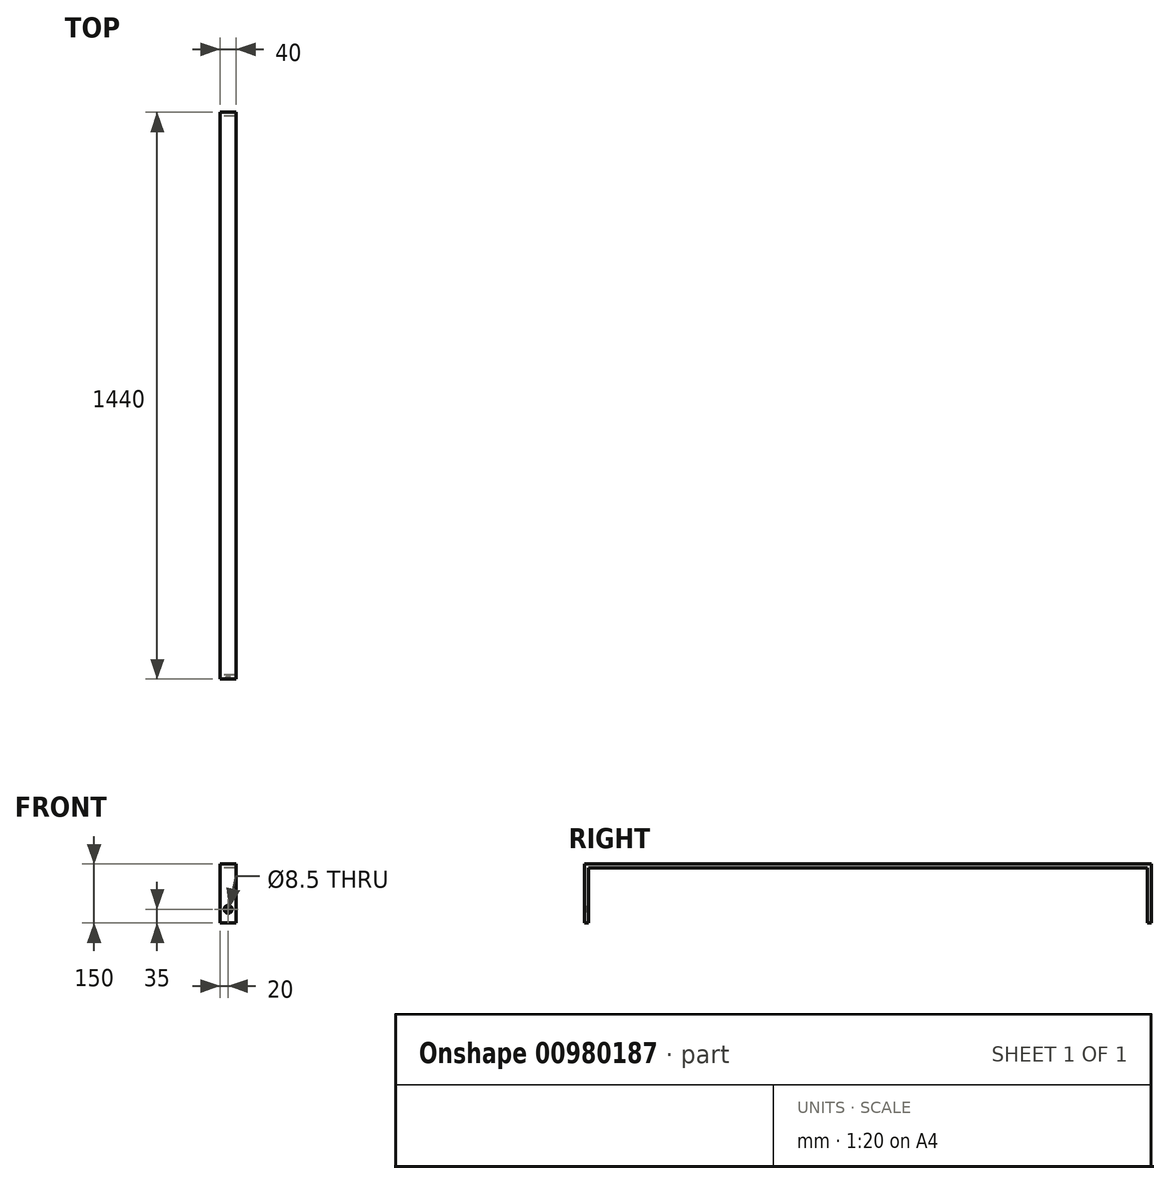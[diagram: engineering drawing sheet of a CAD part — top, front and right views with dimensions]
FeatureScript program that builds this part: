
annotation { "Feature Type Name" : "Feature", "Feature Type Description" : "" }
export const myFeature = defineFeature(function(context is Context, id is Id, definition is map)
    precondition{}
    {
        {
            var Q0;
            Q0=qCreatedBy(makeId("Right.planeOp"),FACE);
            var sketch = newSketch(context, id + "F0", { "sketchPlane" : qUnion([Q0])});
            skLineSegment(sketch, "E0", {"start": v(0, 0) * mm, "end": v(-720, 0) * mm});
            skLineSegment(sketch, "E1", {"start": v(-720, 0) * mm, "end": v(-720, -150) * mm});
            skLineSegment(sketch, "E2", {"start": v(-720, -150) * mm, "end": v(-710, -150) * mm});
            skLineSegment(sketch, "E3", {"start": v(-710, -150) * mm, "end": v(-710, -10) * mm});
            skLineSegment(sketch, "E4", {"start": v(-710, -10) * mm, "end": v(0, -10) * mm});
            skLineSegment(sketch, "E5.MirrorCS", {"start": v(720, -150) * mm, "end": v(710, -150) * mm});
            skLineSegment(sketch, "E6.MirrorCS", {"start": v(710, -150) * mm, "end": v(710, -10) * mm});
            skLineSegment(sketch, "E7.MirrorCS", {"start": v(710, -10) * mm, "end": v(0, -10) * mm});
            skLineSegment(sketch, "E8.MirrorCS", {"start": v(720, 0) * mm, "end": v(720, -150) * mm});
            skLineSegment(sketch, "E9.MirrorCS", {"start": v(0, 0) * mm, "end": v(720, 0) * mm});
            skSolve(sketch);
        }
        {
            var Q0;
            Q0=makeQuery(id+"F0.imprint","IMPRINT",FACE,{"disambiguationData":[TD([[makeQuery(id+"F0.imprint","IMPRINT",EDGE,{"derivedFrom":sQuery(id+"F0.wireOp",EDGE,"E0")}),1.0]])]});
            extrude(context, id + "F1", {"entities" : qUnion([Q0]), "endBound" : BoundingType.SYMMETRIC, "depth" : 40 * mm, "offsetDistance" : 25 * mm});
        }
        {
            var Q0;
            Q0=makeQuery(id+"F1.opExtrude","SWEPT_FACE",FACE,{"disambiguationData":[OSD([sQuery(id+"F0.wireOp",EDGE,"E1")])]});
            var sketch = newSketch(context, id + "F2", { "sketchPlane" : qUnion([Q0])});
            skPoint(sketch, "E10", {"position": v(0, -115) * mm});
            skSolve(sketch);
        }
        {
            var Q0;
            Q0=sQuery(id+"F2.wireOp",VERTEX,"E10");
            var Q1;
            Q1=makeQuery(id+"F1.opExtrude","SWEPT_BODY",BODY,{"disambiguationData":[OSD([sQuery(id+"F0.wireOp",EDGE,"E0"),sQuery(id+"F0.wireOp",EDGE,"E1"),sQuery(id+"F0.wireOp",EDGE,"E2"),sQuery(id+"F0.wireOp",EDGE,"E3"),sQuery(id+"F0.wireOp",EDGE,"E4"),sQuery(id+"F0.wireOp",EDGE,"E5.MirrorCS"),sQuery(id+"F0.wireOp",EDGE,"E6.MirrorCS"),sQuery(id+"F0.wireOp",EDGE,"E7.MirrorCS"),sQuery(id+"F0.wireOp",EDGE,"E8.MirrorCS"),sQuery(id+"F0.wireOp",EDGE,"E9.MirrorCS")])]});
            hole(context, id + "F3", {"style" : HoleStyle.C_SINK, "endStyle" : HoleEndStyle.BLIND, "holeDiameter" : 8.5 * mm, "cSinkDiameter" : 20 * mm, "cSinkAngle" : 90 * degree, "majorDiameter" : 5 * mm, "holeDepth" : 15 * mm, "isTappedThrough" : true, "tappedDepth" : 12 * mm, "tapClearance" : 3, "locations" : qUnion([Q0]), "scope" : qUnion([Q1])});
        }
    });
